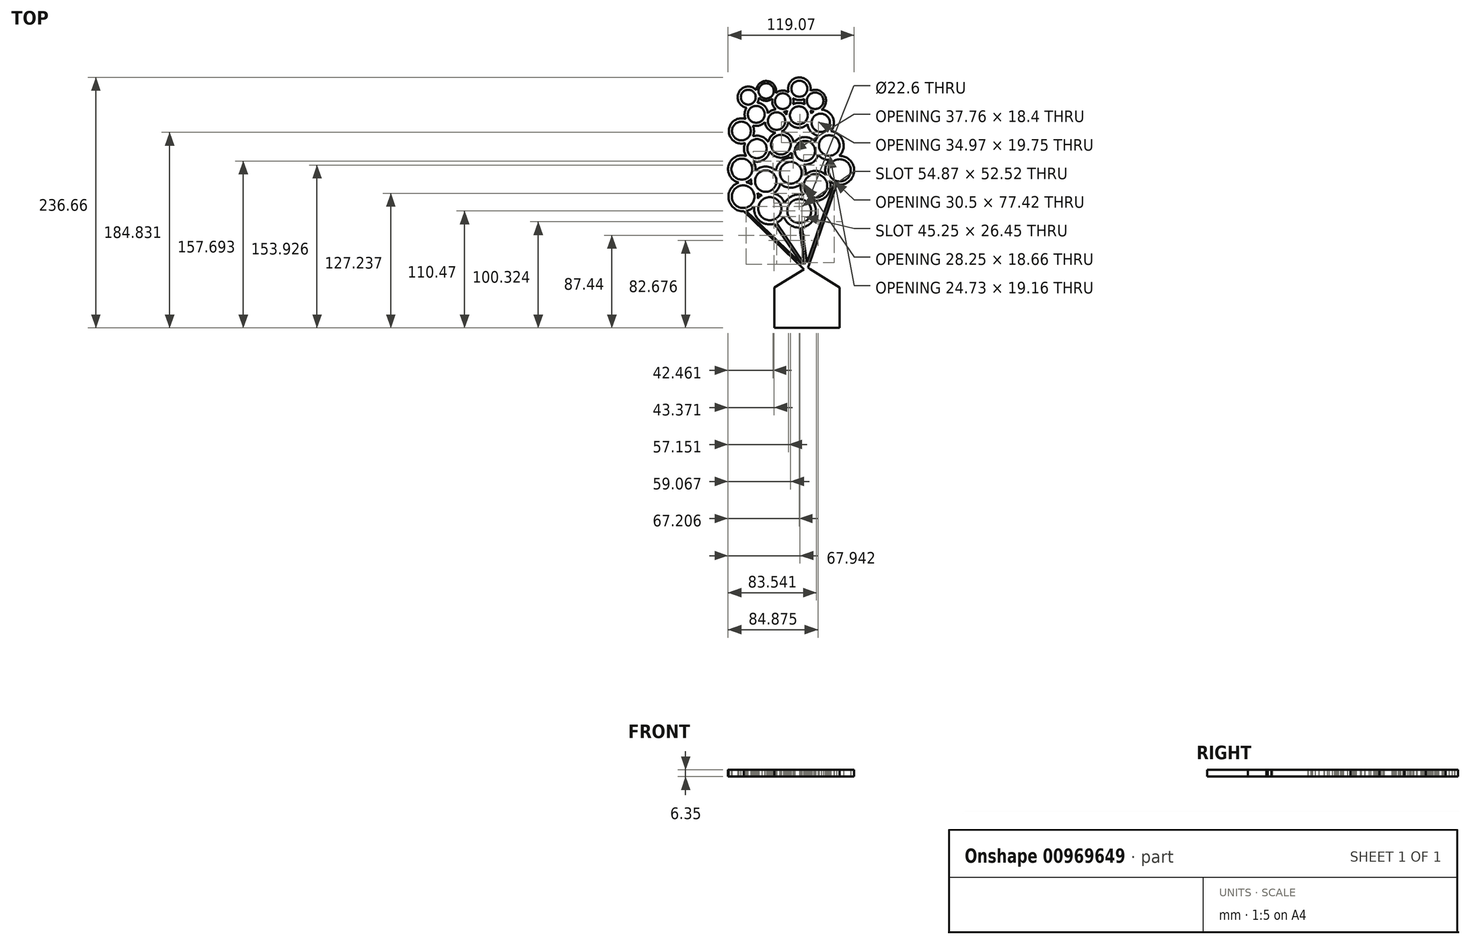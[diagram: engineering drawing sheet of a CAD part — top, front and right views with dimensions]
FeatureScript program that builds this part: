
annotation { "Feature Type Name" : "Feature", "Feature Type Description" : "" }
export const myFeature = defineFeature(function(context is Context, id is Id, definition is map)
    precondition{}
    {
        {
            var Q0;
            Q0=qCreatedBy(makeId("Top.planeOp"),FACE);
            var sketch = newSketch(context, id + "F0", { "sketchPlane" : qUnion([Q0])});
            skCircle(sketch, "E0", {"center": v(-32.6, 24.16) * mm, "radius": 7 * mm});
            skCircle(sketch, "E1", {"center": v(-15.7, 30.07) * mm, "radius": 7.2 * mm});
            skCircle(sketch, "E2", {"center": v(0, 20.38) * mm, "radius": 7.4 * mm});
            skCircle(sketch, "E3", {"center": v(15.64, 32.13) * mm, "radius": 7.6 * mm});
            skCircle(sketch, "E4", {"center": v(-25.06, 7.96) * mm, "radius": 8 * mm});
            skCircle(sketch, "E5", {"center": v(-5.86, 1.6) * mm, "radius": 8.22 * mm});
            skCircle(sketch, "E6", {"center": v(15.17, 7) * mm, "radius": 8.45 * mm});
            skCircle(sketch, "E7", {"center": v(30.48, 20.82) * mm, "radius": 7.8 * mm});
            skArc(sketch, "E8", {"start": v(-24, 18.94) * mm, "mid": v(-23, 21.18) * mm, "end": v(-22.56, 23.6) * mm});
            skArc(sketch, "E9", {"start": v(-6.51, 28.03) * mm, "mid": v(-12.94, 39.08) * mm, "end": v(-24.47, 33.55) * mm});
            skArc(sketch, "E10", {"start": v(0.8, 10.37) * mm, "mid": v(2.53, 10.66) * mm, "end": v(4.19, 11.25) * mm});
            skArc(sketch, "E11", {"start": v(26.13, 30.2) * mm, "mid": v(14.9, 42.77) * mm, "end": v(5.5, 28.78) * mm});
            skArc(sketch, "E12", {"start": v(-14.08, 8.94) * mm, "mid": v(-17.23, 15.73) * mm, "end": v(-24, 18.94) * mm});
            skArc(sketch, "E13", {"start": v(3.4, 7.55) * mm, "mid": v(2.23, 9.07) * mm, "end": v(0.8, 10.37) * mm});
            skArc(sketch, "E14", {"start": v(26.83, 8.69) * mm, "mid": v(26.53, 10.1) * mm, "end": v(26.07, 11.47) * mm});
            skArc(sketch, "E15", {"start": v(26.07, 11.47) * mm, "mid": v(27.58, 10.9) * mm, "end": v(29.16, 10.57) * mm});
            skCircle(sketch, "E16", {"center": v(35.77, 0) * mm, "radius": 8.65 * mm});
            skCircle(sketch, "E17", {"center": v(-39.07, -7.77) * mm, "radius": 8.85 * mm});
            skCircle(sketch, "E18", {"center": v(-24.39, -24.5) * mm, "radius": 9.1 * mm});
            skCircle(sketch, "E19", {"center": v(-1.8, -20.67) * mm, "radius": 9.3 * mm});
            skCircle(sketch, "E20", {"center": v(20.93, -26.6) * mm, "radius": 9.5 * mm});
            skCircle(sketch, "E21", {"center": v(43.83, -21.5) * mm, "radius": 9.7 * mm});
            skCircle(sketch, "E22", {"center": v(-38.67, -43.84) * mm, "radius": 9.9 * mm});
            skCircle(sketch, "E23", {"center": v(-16.1, -55.15) * mm, "radius": 10.1 * mm});
            skCircle(sketch, "E24", {"center": v(7.52, -47.23) * mm, "radius": 10.3 * mm});
            skArc(sketch, "E25", {"start": v(-28.3, -12.83) * mm, "mid": v(-27.17, -7.68) * mm, "end": v(-28.37, -2.55) * mm});
            skArc(sketch, "E26", {"start": v(-28.11, -36.21) * mm, "mid": v(-18.17, -35.1) * mm, "end": v(-12.34, -26.97) * mm});
            skArc(sketch, "E27", {"start": v(-12.34, -26.97) * mm, "mid": v(-2.5, -32.94) * mm, "end": v(7.96, -28.14) * mm});
            skArc(sketch, "E28", {"start": v(7.96, -28.14) * mm, "mid": v(8.55, -30.75) * mm, "end": v(9.65, -33.18) * mm});
            skArc(sketch, "E29", {"start": v(33.43, -30.35) * mm, "mid": v(38.28, -33.98) * mm, "end": v(44.22, -35.15) * mm});
            skArc(sketch, "E30", {"start": v(-34.62, -56.21) * mm, "mid": v(-32, -55.02) * mm, "end": v(-29.7, -53.28) * mm});
            skArc(sketch, "E31", {"start": v(-23.97, -66.4) * mm, "mid": v(-22, -67.55) * mm, "end": v(-19.87, -68.36) * mm});
            skArc(sketch, "E32", {"start": v(-2.52, -57.3) * mm, "mid": v(6.98, -61.43) * mm, "end": v(16.77, -58.02) * mm});
            skArc(sketch, "E33", {"start": v(45.38, -7.93) * mm, "mid": v(47.2, 4.96) * mm, "end": v(36.54, 12.44) * mm});
            skCircle(sketch, "E34", {"center": v(30.86, -59.63) * mm, "radius": 11.1 * mm});
            skCircle(sketch, "E35", {"center": v(53.7, -45) * mm, "radius": 10.5 * mm});
            skCircle(sketch, "E36", {"center": v(-37.42, -69.8) * mm, "radius": 10.7 * mm});
            skCircle(sketch, "E37", {"center": v(-12.26, -81.19) * mm, "radius": 10.9 * mm});
            skCircle(sketch, "E38", {"center": v(15.52, -83.4) * mm, "radius": 11.3 * mm});
            skArc(sketch, "E39", {"start": v(40.8, -49.52) * mm, "mid": v(31.35, -45.46) * mm, "end": v(21.63, -48.86) * mm});
            skArc(sketch, "E40", {"start": v(44.2, -54.83) * mm, "mid": v(46.2, -56.42) * mm, "end": v(48.43, -57.6) * mm});
            skArc(sketch, "E41", {"start": v(-23.65, -71.56) * mm, "mid": v(-23.57, -68.97) * mm, "end": v(-23.97, -66.4) * mm});
            skArc(sketch, "E42", {"start": v(1.7, -75.95) * mm, "mid": v(-2.34, -70.05) * mm, "end": v(-8.67, -66.7) * mm});
            skArc(sketch, "E43", {"start": v(19.59, -68.25) * mm, "mid": v(9.3, -68.99) * mm, "end": v(1.7, -75.95) * mm});
            skLineSegment(sketch, "E44", {"start": v(50.9, -58.38) * mm, "end": v(25, -133.4) * mm});
            skArc(sketch, "E45.trimOffspring", {"start": v(27.65, -73.45) * mm, "mid": v(41.46, -69.06) * mm, "end": v(44.2, -54.83) * mm});
            skArc(sketch, "E46.trimOffspring", {"start": v(0.7, -88.56) * mm, "mid": v(6.5, -96.22) * mm, "end": v(15.68, -99.07) * mm});
            skArc(sketch, "E47.trimOffspring", {"start": v(-27.02, -78.99) * mm, "mid": v(-22.03, -92.46) * mm, "end": v(-7.98, -95.48) * mm});
            skArc(sketch, "E48.trimOffspring", {"start": v(-29.42, -58.46) * mm, "mid": v(-31.9, -57.07) * mm, "end": v(-34.62, -56.21) * mm});
            skArc(sketch, "E49.trimOffspring", {"start": v(-6.56, -45.26) * mm, "mid": v(-16.17, -41.41) * mm, "end": v(-25.74, -45.37) * mm});
            skArc(sketch, "E50.trimOffspring", {"start": v(-41.5, -56.54) * mm, "mid": v(-51.1, -72.09) * mm, "end": v(-36.99, -83.67) * mm});
            skArc(sketch, "E51.trimOffspring", {"start": v(-34.5, -31.5) * mm, "mid": v(-51.2, -40.32) * mm, "end": v(-41.5, -56.54) * mm});
            skArc(sketch, "E52.trimOffspring", {"start": v(-13.83, -18.2) * mm, "mid": v(-20.12, -12.96) * mm, "end": v(-28.3, -12.83) * mm});
            skArc(sketch, "E53.trimOffspring", {"start": v(10.37, -18.9) * mm, "mid": v(6.46, -11.56) * mm, "end": v(-1.23, -8.4) * mm});
            skArc(sketch, "E54.trimOffspring", {"start": v(-35.44, -19.1) * mm, "mid": v(-36.65, -25.43) * mm, "end": v(-34.5, -31.5) * mm});
            skArc(sketch, "E55.trimOffspring", {"start": v(16.77, -58.02) * mm, "mid": v(17.19, -63.4) * mm, "end": v(19.59, -68.25) * mm});
            skArc(sketch, "E56.trimOffspring", {"start": v(21.63, -48.86) * mm, "mid": v(21.36, -44.03) * mm, "end": v(19.49, -39.57) * mm});
            skArc(sketch, "E57.trimOffspring", {"start": v(30.66, -17.88) * mm, "mid": v(20.27, -13.55) * mm, "end": v(10.37, -18.9) * mm});
            skArc(sketch, "E58.trimOffspring", {"start": v(33.73, -12.3) * mm, "mid": v(31.87, -14.9) * mm, "end": v(30.66, -17.88) * mm});
            skArc(sketch, "E59.trimOffspring", {"start": v(23.39, -1.44) * mm, "mid": v(26.75, -8.6) * mm, "end": v(33.73, -12.3) * mm});
            skArc(sketch, "E60.trimOffspring", {"start": v(20.73, 17.38) * mm, "mid": v(15.15, 18.78) * mm, "end": v(9.58, 17.37) * mm});
            skArc(sketch, "E61.trimOffspring", {"start": v(5.13, 0.85) * mm, "mid": v(13.7, -4.69) * mm, "end": v(23.39, -1.44) * mm});
            skArc(sketch, "E62.trimOffspring", {"start": v(-16.83, 0.62) * mm, "mid": v(-13.59, -6.25) * mm, "end": v(-6.66, -9.39) * mm});
            skArc(sketch, "E63.trimOffspring", {"start": v(-6.36, 12.6) * mm, "mid": v(-10.59, 11.55) * mm, "end": v(-14.08, 8.94) * mm});
            skArc(sketch, "E64.trimOffspring", {"start": v(-28.37, -2.55) * mm, "mid": v(-22.14, -2.67) * mm, "end": v(-16.83, 0.62) * mm});
            skArc(sketch, "E65.trimOffspring", {"start": v(-35.13, 3.46) * mm, "mid": v(-50.97, -7.6) * mm, "end": v(-35.44, -19.1) * mm});
            skArc(sketch, "E66.trimOffspring", {"start": v(-34.15, 14.22) * mm, "mid": v(-36.04, 8.97) * mm, "end": v(-35.13, 3.46) * mm});
            skArc(sketch, "E67.trimOffspring", {"start": v(9.58, 17.37) * mm, "mid": v(10.04, 20.35) * mm, "end": v(9.6, 23.33) * mm});
            skArc(sketch, "E68.trimOffspring", {"start": v(4.19, 11.25) * mm, "mid": v(3.65, 9.43) * mm, "end": v(3.4, 7.55) * mm});
            skArc(sketch, "E69.trimOffspring", {"start": v(20.28, 22.52) * mm, "mid": v(20.18, 19.92) * mm, "end": v(20.73, 17.38) * mm});
            skArc(sketch, "E70.trimOffspring", {"start": v(9.6, 23.33) * mm, "mid": v(14.83, 21.49) * mm, "end": v(20.28, 22.52) * mm});
            skArc(sketch, "E71.trimOffspring", {"start": v(5.5, 28.78) * mm, "mid": v(-0.63, 30.4) * mm, "end": v(-6.51, 28.03) * mm});
            skArc(sketch, "E72.trimOffspring", {"start": v(-9.76, 22.77) * mm, "mid": v(-9.53, 17.2) * mm, "end": v(-6.36, 12.6) * mm});
            skArc(sketch, "E73.trimOffspring", {"start": v(-25.1, 30.86) * mm, "mid": v(-41.45, 28.96) * mm, "end": v(-34.15, 14.22) * mm});
            skArc(sketch, "E74.trimOffspring", {"start": v(-22.56, 23.6) * mm, "mid": v(-16.32, 20.67) * mm, "end": v(-9.76, 22.77) * mm});
            skArc(sketch, "E75.trimOffspring", {"start": v(53.31, -31.32) * mm, "mid": v(56.76, -17.11) * mm, "end": v(45.38, -7.93) * mm});
            skArc(sketch, "E76.trimOffspring", {"start": v(44.22, -35.15) * mm, "mid": v(40.4, -41.83) * mm, "end": v(40.8, -49.52) * mm});
            skArc(sketch, "E77.trimOffspring", {"start": v(9.65, -33.18) * mm, "mid": v(-0.97, -35.83) * mm, "end": v(-6.56, -45.26) * mm});
            skArc(sketch, "E78.trimOffspring", {"start": v(19.49, -39.57) * mm, "mid": v(28.13, -37.49) * mm, "end": v(33.43, -30.35) * mm});
            skArc(sketch, "E79.trimOffspring", {"start": v(-19.87, -68.36) * mm, "mid": v(-21.9, -69.8) * mm, "end": v(-23.65, -71.56) * mm});
            skArc(sketch, "E80.trimOffspring", {"start": v(-8.67, -66.7) * mm, "mid": v(-4.59, -62.66) * mm, "end": v(-2.52, -57.3) * mm});
            skLineSegment(sketch, "E81", {"start": v(48.43, -57.6) * mm, "end": v(22.66, -132.24) * mm});
            skLineSegment(sketch, "E82", {"start": v(22.66, -132.24) * mm, "end": v(17.94, -98.89) * mm});
            skLineSegment(sketch, "E83", {"start": v(15.68, -99.07) * mm, "end": v(20.6, -133.81) * mm});
            skLineSegment(sketch, "E84", {"start": v(20.6, -133.81) * mm, "end": v(-5.85, -94.66) * mm});
            skLineSegment(sketch, "E85", {"start": v(-7.98, -95.48) * mm, "end": v(17.94, -133.85) * mm});
            skLineSegment(sketch, "E86", {"start": v(17.94, -133.85) * mm, "end": v(-34.58, -83.39) * mm});
            skLineSegment(sketch, "E87", {"start": v(-36.99, -83.67) * mm, "end": v(19.93, -138.36) * mm});
            skArc(sketch, "E88.trimOffspring", {"start": v(-5.85, -94.66) * mm, "mid": v(-2.1, -92.11) * mm, "end": v(0.7, -88.56) * mm});
            skArc(sketch, "E89.trimOffspring", {"start": v(17.94, -98.89) * mm, "mid": v(30.17, -88.98) * mm, "end": v(27.65, -73.45) * mm});
            skArc(sketch, "E90.trimOffspring", {"start": v(-34.58, -83.39) * mm, "mid": v(-30.44, -81.8) * mm, "end": v(-27.02, -78.99) * mm});
            skArc(sketch, "E91.trimOffspring", {"start": v(50.9, -58.38) * mm, "mid": v(67.33, -46.2) * mm, "end": v(53.31, -31.32) * mm});
            skLineSegment(sketch, "E92", {"start": v(19.93, -138.36) * mm, "end": v(-8.14, -155.76) * mm});
            skPoint(sketch, "E92.startSnap0", {"position": v(23.6, -136.94) * mm});
            skLineSegment(sketch, "E93", {"start": v(52.75, -155.6) * mm, "end": v(53.65, -155.6) * mm});
            skLineSegment(sketch, "E94", {"start": v(53.65, -155.6) * mm, "end": v(25.58, -138.2) * mm});
            skArc(sketch, "E95.trimOffspring", {"start": v(-6.66, -9.39) * mm, "mid": v(-11.32, -12.91) * mm, "end": v(-13.83, -18.2) * mm});
            skArc(sketch, "E96.trimOffspring", {"start": v(-1.23, -8.4) * mm, "mid": v(3.21, -4.64) * mm, "end": v(5.13, 0.85) * mm});
            skArc(sketch, "E97", {"start": v(-24.85, 32.37) * mm, "mid": v(-24.85, 32.37) * mm, "end": v(-24.85, 32.37) * mm});
            skArc(sketch, "E98", {"start": v(-24.47, 33.55) * mm, "mid": v(-24.88, 32.23) * mm, "end": v(-25.1, 30.86) * mm});
            skPoint(sketch, "E99", {"position": v(-28.4, 33.3) * mm});
            skPoint(sketch, "E100", {"position": v(-26.77, 32.36) * mm});
            skLineSegment(sketch, "E101.top", {"start": v(-8.14, -193.86) * mm, "end": v(53.65, -193.86) * mm});
            skLineSegment(sketch, "E101.left", {"start": v(-8.14, -155.76) * mm, "end": v(-8.14, -193.86) * mm});
            skLineSegment(sketch, "E102", {"start": v(53.65, -155.6) * mm, "end": v(53.65, -193.86) * mm});
            skLineSegment(sketch, "E103", {"start": v(25, -133.4) * mm, "end": v(23.6, -136.94) * mm});
            skLineSegment(sketch, "E104", {"start": v(25.58, -138.2) * mm, "end": v(23.6, -136.94) * mm});
            skArc(sketch, "E105.trimOffspring", {"start": v(-29.7, -53.28) * mm, "mid": v(-29.8, -55.88) * mm, "end": v(-29.42, -58.46) * mm});
            skArc(sketch, "E106.trimOffspring", {"start": v(-25.74, -45.37) * mm, "mid": v(-26.06, -40.57) * mm, "end": v(-28.11, -36.21) * mm});
            skArc(sketch, "E107.trimOffspring", {"start": v(36.54, 12.44) * mm, "mid": v(39.4, 26.05) * mm, "end": v(26.13, 30.2) * mm});
            skArc(sketch, "E108.trimOffspring", {"start": v(29.16, 10.57) * mm, "mid": v(27.94, 9.7) * mm, "end": v(26.83, 8.69) * mm});
            skSolve(sketch);
        }
        {
            var Q0;
            Q0=makeQuery(id+"F0.imprint","IMPRINT",FACE,{"disambiguationData":[TD([[makeQuery(id+"F0.imprint","IMPRINT",EDGE,{"derivedFrom":sQuery(id+"F0.wireOp",EDGE,"E0")}),-1.0]])]});
            extrude(context, id + "F1", {"entities" : qUnion([Q0]), "depth" : 6.35 * mm});
        }
    });
